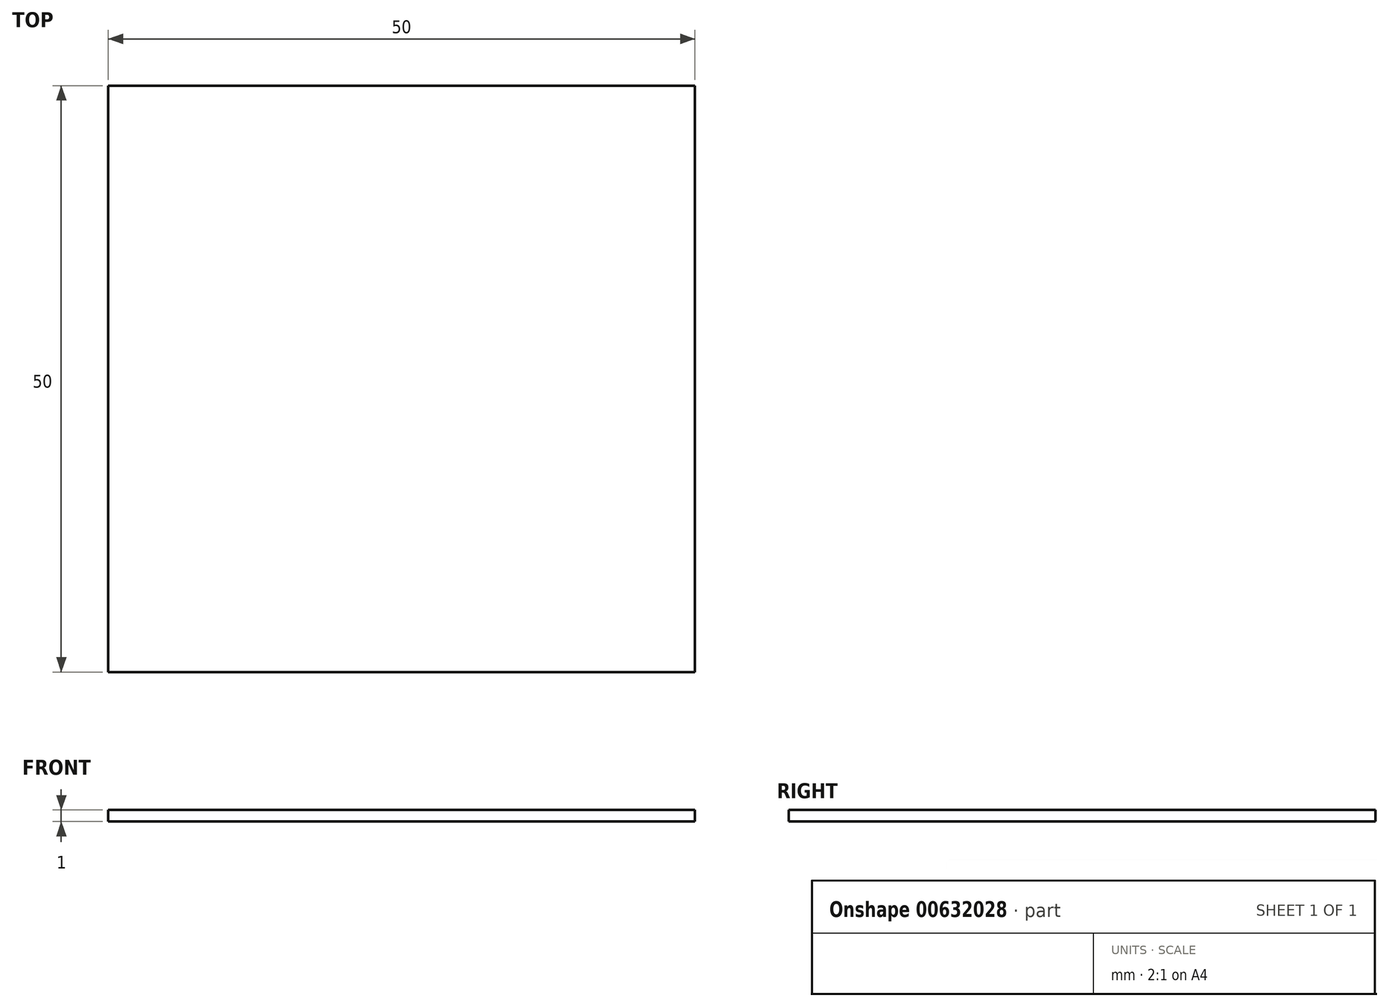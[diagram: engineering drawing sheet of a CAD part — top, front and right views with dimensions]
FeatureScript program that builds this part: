
annotation { "Feature Type Name" : "Feature", "Feature Type Description" : "" }
export const myFeature = defineFeature(function(context is Context, id is Id, definition is map)
    precondition{}
    {
        {
            var Q0;
            Q0=qCreatedBy(makeId("Top.planeOp"),FACE);
            var sketch = newSketch(context, id + "F0", { "sketchPlane" : qUnion([Q0])});
            skLineSegment(sketch, "E0.bottom", {"start": v(25, 25) * mm, "end": v(-25, 25) * mm});
            skLineSegment(sketch, "E0.top", {"start": v(25, -25) * mm, "end": v(-25, -25) * mm});
            skLineSegment(sketch, "E0.left", {"start": v(25, 25) * mm, "end": v(25, -25) * mm});
            skLineSegment(sketch, "E0.right", {"start": v(-25, 25) * mm, "end": v(-25, -25) * mm});
            skPoint(sketch, "E0.middle", {"position": v(0, 0) * mm});
            skSolve(sketch);
        }
        {
            var Q0;
            Q0 = qSketchRegion(id + "F0", true);
            extrude(context, id + "F1", {"entities" : qUnion([Q0]), "depth" : 1 * mm, "offsetDistance" : 25 * mm});
        }
    });
